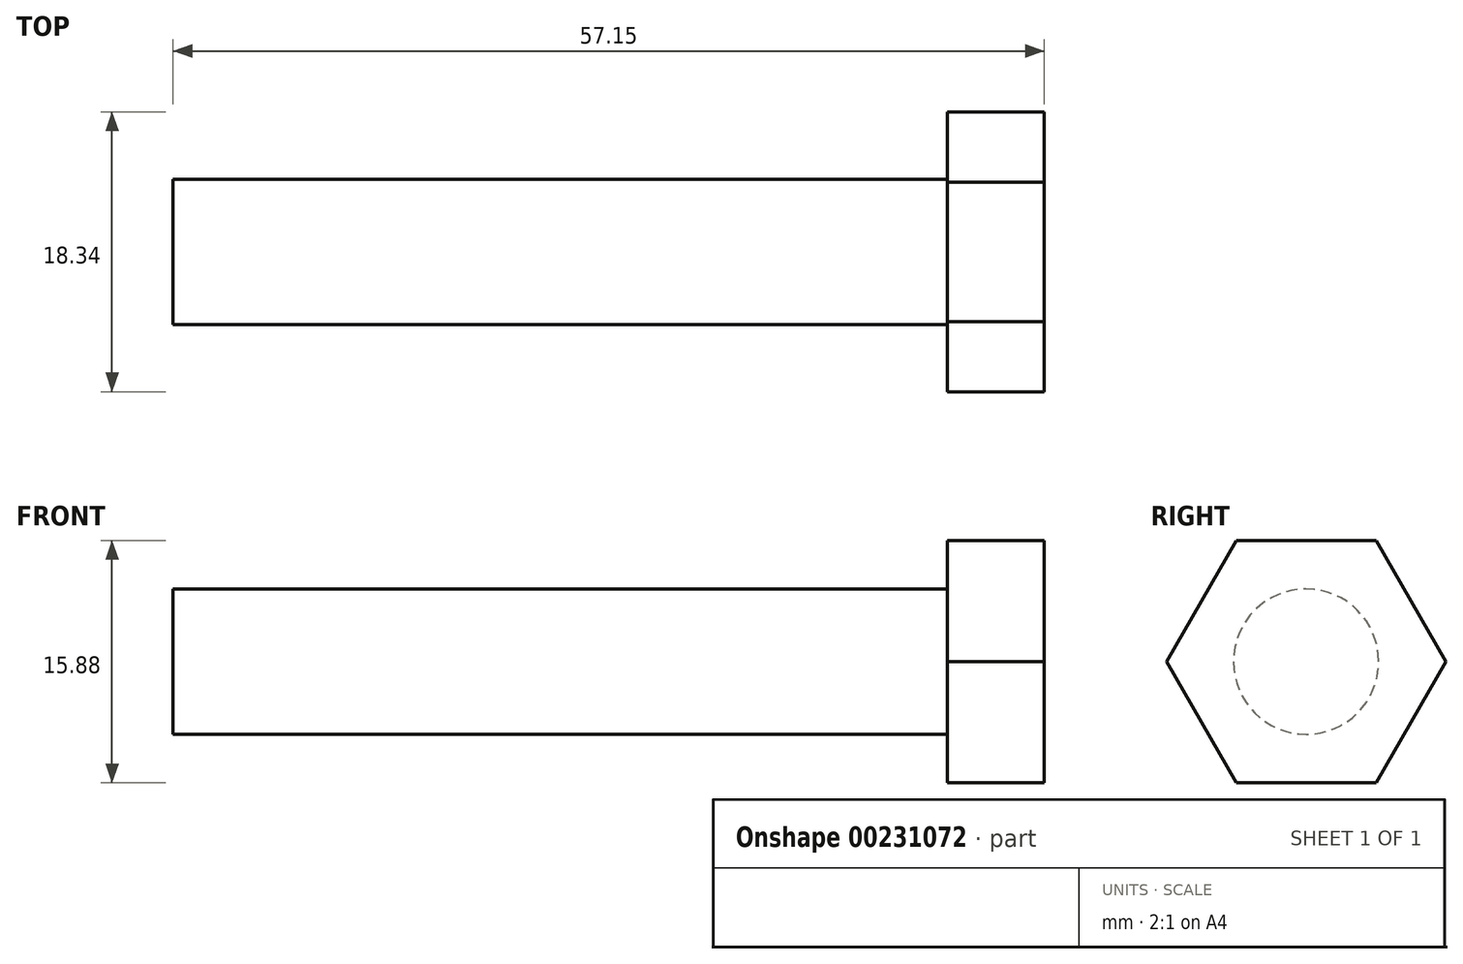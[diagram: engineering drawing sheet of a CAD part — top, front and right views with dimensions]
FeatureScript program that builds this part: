
annotation { "Feature Type Name" : "Feature", "Feature Type Description" : "" }
export const myFeature = defineFeature(function(context is Context, id is Id, definition is map)
    precondition{}
    {
        {
            var Q0;
            Q0=qCreatedBy(makeId("Right.planeOp"),FACE);
            var sketch = newSketch(context, id + "F0", { "sketchPlane" : qUnion([Q0])});
            skCircle(sketch, "E0", {"center": v(0, 0) * mm, "radius": 4.76 * mm});
            skSolve(sketch);
        }
        {
            var Q0;
            Q0 = qSketchRegion(id + "F0", true);
            extrude(context, id + "F1", {"entities" : qUnion([Q0]), "depth" : 50.8 * mm});
        }
        {
            var Q0;
            Q0=makeQuery(id+"F1.opExtrude","CAP_FACE",FACE,{"disambiguationData":[OSD([sQuery(id+"F0.wireOp",EDGE,"E0")])],"isStart":false});
            var sketch = newSketch(context, id + "F2", { "sketchPlane" : qUnion([Q0])});
            skCircle(sketch, "E1.cCircle", {"center": v(0, 0) * mm, "radius": 7.94 * mm, "construction": true});
            skLineSegment(sketch, "E1.0", {"start": v(-4.58, 7.94) * mm, "end": v(4.58, 7.94) * mm});
            skLineSegment(sketch, "E1.1", {"start": v(4.58, 7.94) * mm, "end": v(9.17, 0) * mm});
            skLineSegment(sketch, "E1.2", {"start": v(9.17, 0) * mm, "end": v(4.58, -7.94) * mm});
            skLineSegment(sketch, "E1.3", {"start": v(4.58, -7.94) * mm, "end": v(-4.58, -7.94) * mm});
            skLineSegment(sketch, "E1.4", {"start": v(-4.58, -7.94) * mm, "end": v(-9.17, 0) * mm});
            skLineSegment(sketch, "E1.5", {"start": v(-9.17, 0) * mm, "end": v(-4.58, 7.94) * mm});
            skPoint(sketch, "E1.0.midPoint", {"position": v(0, 7.94) * mm});
            skSolve(sketch);
        }
        {
            var Q0;
            Q0 = qSketchRegion(id + "F2", true);
            extrude(context, id + "F3", {"entities" : qUnion([Q0]), "operationType" : NewBodyOperationType.ADD, "depth" : 6.35 * mm});
        }
    });
